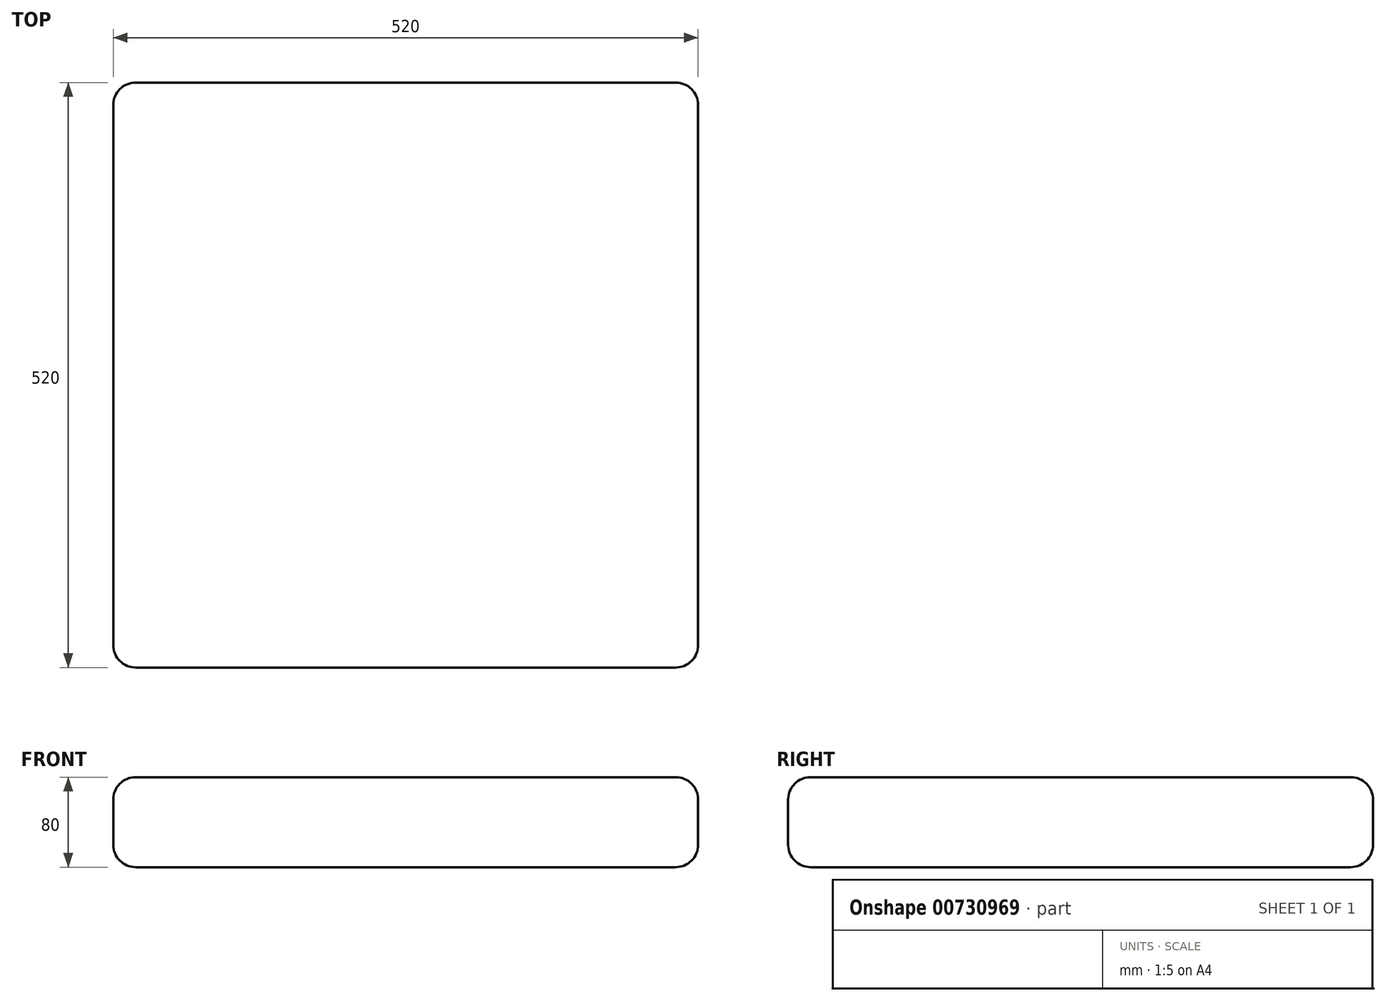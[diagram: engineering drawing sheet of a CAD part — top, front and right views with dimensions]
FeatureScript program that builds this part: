
annotation { "Feature Type Name" : "Feature", "Feature Type Description" : "" }
export const myFeature = defineFeature(function(context is Context, id is Id, definition is map)
    precondition{}
    {
        {
            var Q0;
            Q0=qCreatedBy(makeId("Top.planeOp"),FACE);
            var sketch = newSketch(context, id + "F0", { "sketchPlane" : qUnion([Q0])});
            skLineSegment(sketch, "E0.bottom", {"start": v(260, -260) * mm, "end": v(-260, -260) * mm});
            skLineSegment(sketch, "E0.top", {"start": v(260, 260) * mm, "end": v(-260, 260) * mm});
            skLineSegment(sketch, "E0.left", {"start": v(260, -260) * mm, "end": v(260, 260) * mm});
            skLineSegment(sketch, "E0.right", {"start": v(-260, -260) * mm, "end": v(-260, 260) * mm});
            skPoint(sketch, "E0.middle", {"position": v(0, 0) * mm});
            skSolve(sketch);
        }
        {
            var Q0;
            Q0=makeQuery(id+"F0.imprint","IMPRINT",FACE,{"disambiguationData":[TD([[makeQuery(id+"F0.imprint","IMPRINT",EDGE,{"derivedFrom":sQuery(id+"F0.wireOp",EDGE,"E0.bottom")}),-1.0]])]});
            extrude(context, id + "F1", {"entities" : qUnion([Q0]), "depth" : 80 * mm, "offsetDistance" : 25 * mm});
        }
        {
            var Q0;
            Q0=makeQuery(id+"F1.opExtrude","CAP_EDGE",EDGE,{"disambiguationData":[OSD([sQuery(id+"F0.wireOp",EDGE,"E0.left")])],"isStart":false});
            var Q1;
            Q1=makeQuery(id+"F1.opExtrude","CAP_EDGE",EDGE,{"disambiguationData":[OSD([sQuery(id+"F0.wireOp",EDGE,"E0.top")])],"isStart":false});
            var Q2;
            Q2=makeQuery(id+"F1.opExtrude","CAP_EDGE",EDGE,{"disambiguationData":[OSD([sQuery(id+"F0.wireOp",EDGE,"E0.right")])],"isStart":false});
            var Q3;
            Q3=makeQuery(id+"F1.opExtrude","CAP_EDGE",EDGE,{"disambiguationData":[OSD([sQuery(id+"F0.wireOp",EDGE,"E0.bottom")])],"isStart":false});
            var Q4;
            Q4=makeQuery(id+"F1.opExtrude","CAP_EDGE",EDGE,{"disambiguationData":[OSD([sQuery(id+"F0.wireOp",EDGE,"E0.bottom")])],"isStart":true});
            var Q5;
            Q5=makeQuery(id+"F1.opExtrude","CAP_EDGE",EDGE,{"disambiguationData":[OSD([sQuery(id+"F0.wireOp",EDGE,"E0.left")])],"isStart":true});
            var Q6;
            Q6=makeQuery(id+"F1.opExtrude","CAP_EDGE",EDGE,{"disambiguationData":[OSD([sQuery(id+"F0.wireOp",EDGE,"E0.top")])],"isStart":true});
            var Q7;
            Q7=makeQuery(id+"F1.opExtrude","CAP_EDGE",EDGE,{"disambiguationData":[OSD([sQuery(id+"F0.wireOp",EDGE,"E0.right")])],"isStart":true});
            fillet(context, id + "F2", {"entities" : qUnion([Q0, Q1, Q2, Q3, Q4, Q5, Q6, Q7]), "radius" : 20 * mm, "tangentPropagation" : true, "allowEdgeOverflow" : false});
        }
        {
            var Q0;
            Q0=makeQuery(id+"F1.opExtrude","SWEPT_EDGE",EDGE,{"disambiguationData":[OSD([sQuery(id+"F0.wireOp",EDGE,"E0.bottom"),sQuery(id+"F0.wireOp",EDGE,"E0.left")])]});
            var Q1;
            Q1=makeQuery(id+"F1.opExtrude","SWEPT_EDGE",EDGE,{"disambiguationData":[OSD([sQuery(id+"F0.wireOp",EDGE,"E0.top"),sQuery(id+"F0.wireOp",EDGE,"E0.left")])]});
            var Q2;
            Q2=makeQuery(id+"F1.opExtrude","SWEPT_EDGE",EDGE,{"disambiguationData":[OSD([sQuery(id+"F0.wireOp",EDGE,"E0.top"),sQuery(id+"F0.wireOp",EDGE,"E0.right")])]});
            var Q3;
            Q3=makeQuery(id+"F1.opExtrude","SWEPT_EDGE",EDGE,{"disambiguationData":[OSD([sQuery(id+"F0.wireOp",EDGE,"E0.bottom"),sQuery(id+"F0.wireOp",EDGE,"E0.right")])]});
            fillet(context, id + "F3", {"entities" : qUnion([Q0, Q1, Q2, Q3]), "radius" : 20 * mm, "tangentPropagation" : true, "allowEdgeOverflow" : false});
        }
    });
